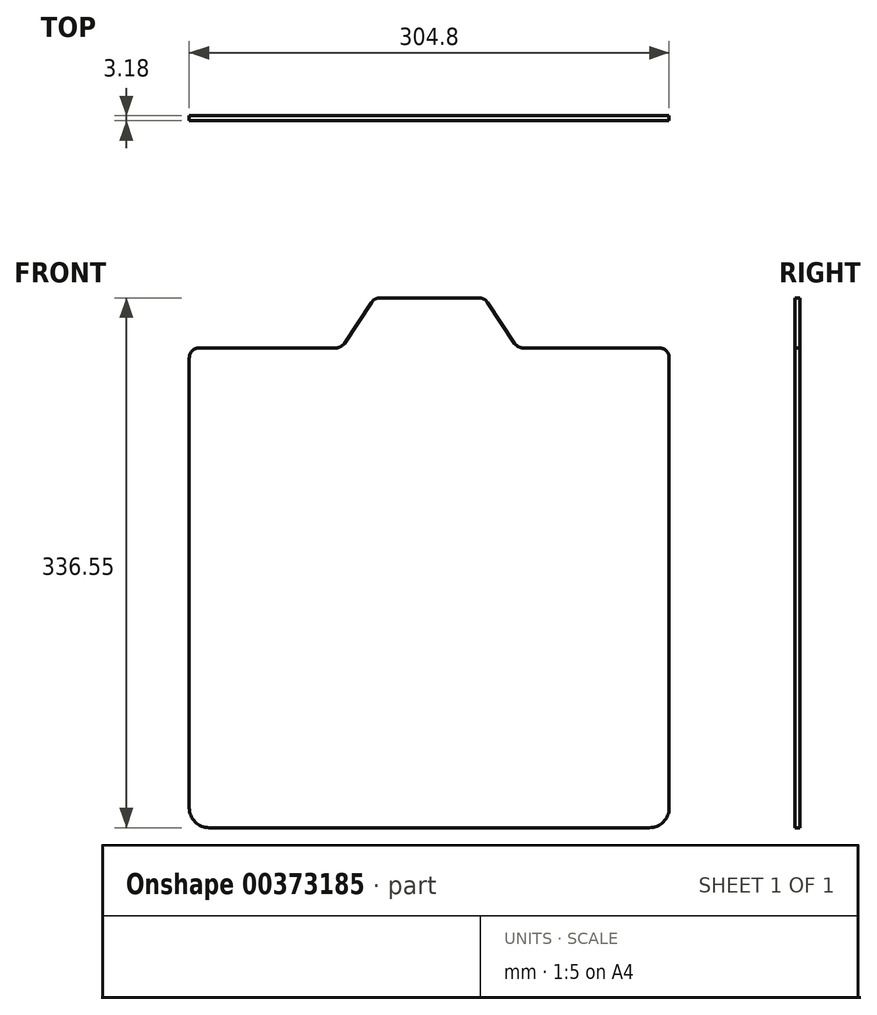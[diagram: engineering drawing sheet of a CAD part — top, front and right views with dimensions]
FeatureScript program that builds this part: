
annotation { "Feature Type Name" : "Feature", "Feature Type Description" : "" }
export const myFeature = defineFeature(function(context is Context, id is Id, definition is map)
    precondition{}
    {
        {
            var Q0;
            Q0=qCreatedBy(makeId("Front.planeOp"),FACE);
            var sketch = newSketch(context, id + "F0", { "sketchPlane" : qUnion([Q0])});
            skLineSegment(sketch, "E0.bottom", {"start": v(-152.4, 152.4) * mm, "end": v(-55.83, 152.4) * mm});
            skLineSegment(sketch, "E0.top", {"start": v(-152.4, -152.4) * mm, "end": v(152.4, -152.4) * mm});
            skLineSegment(sketch, "E0.left", {"start": v(-152.4, 152.4) * mm, "end": v(-152.4, -152.4) * mm});
            skLineSegment(sketch, "E0.right", {"start": v(152.4, 152.4) * mm, "end": v(152.4, -152.4) * mm});
            skPoint(sketch, "E0.middle", {"position": v(0, 0) * mm});
            skLineSegment(sketch, "E1.bottom", {"start": v(-34.77, 184.15) * mm, "end": v(35.08, 184.15) * mm});
            skPoint(sketch, "E1.middle", {"position": v(0, 152.4) * mm});
            skPoint(sketch, "E1.top.start.orphan", {"position": v(-35.08, 120.65) * mm});
            skPoint(sketch, "E2.orphan", {"position": v(34.77, 120.65) * mm});
            skLineSegment(sketch, "E3", {"start": v(35.08, 184.15) * mm, "end": v(56.14, 152.4) * mm});
            skLineSegment(sketch, "E4", {"start": v(-34.77, 184.15) * mm, "end": v(-55.83, 152.4) * mm});
            skLineSegment(sketch, "E5.trimOffspring", {"start": v(56.14, 152.4) * mm, "end": v(152.4, 152.4) * mm});
            skSolve(sketch);
        }
        {
            var Q0;
            Q0=makeQuery(id+"F0.imprint","IMPRINT",FACE,{"disambiguationData":[TD([[makeQuery(id+"F0.imprint","IMPRINT",EDGE,{"derivedFrom":sQuery(id+"F0.wireOp",EDGE,"E0.bottom")}),-1.0]])]});
            extrude(context, id + "F1", {"entities" : qUnion([Q0]), "endBound" : BoundingType.SYMMETRIC, "depth" : 3.17 * mm});
        }
        {
            var Q0;
            Q0=makeQuery(id+"F1.opExtrude","SWEPT_EDGE",EDGE,{"disambiguationData":[OSD([sQuery(id+"F0.wireOp",EDGE,"E0.right"),sQuery(id+"F0.wireOp",EDGE,"E5.trimOffspring")])]});
            var Q1;
            Q1=makeQuery(id+"F1.opExtrude","SWEPT_EDGE",EDGE,{"disambiguationData":[OSD([sQuery(id+"F0.wireOp",EDGE,"E0.bottom"),sQuery(id+"F0.wireOp",EDGE,"E0.left")])]});
            var Q2;
            Q2=makeQuery(id+"F1.opExtrude","SWEPT_EDGE",EDGE,{"disambiguationData":[OSD([sQuery(id+"F0.wireOp",EDGE,"E0.bottom"),sQuery(id+"F0.wireOp",EDGE,"E4")])]});
            var Q3;
            Q3=makeQuery(id+"F1.opExtrude","SWEPT_EDGE",EDGE,{"disambiguationData":[OSD([sQuery(id+"F0.wireOp",EDGE,"E1.bottom"),sQuery(id+"F0.wireOp",EDGE,"E4")])]});
            var Q4;
            Q4=makeQuery(id+"F1.opExtrude","SWEPT_EDGE",EDGE,{"disambiguationData":[OSD([sQuery(id+"F0.wireOp",EDGE,"E1.bottom"),sQuery(id+"F0.wireOp",EDGE,"E3")])]});
            var Q5;
            Q5=makeQuery(id+"F1.opExtrude","SWEPT_EDGE",EDGE,{"disambiguationData":[OSD([sQuery(id+"F0.wireOp",EDGE,"E3"),sQuery(id+"F0.wireOp",EDGE,"E5.trimOffspring")])]});
            fillet(context, id + "F2", {"entities" : qUnion([Q0, Q1, Q2, Q3, Q4, Q5]), "radius" : 6.35 * mm, "tangentPropagation" : true, "allowEdgeOverflow" : false});
        }
        {
            var Q0;
            Q0=makeQuery(id+"F1.opExtrude","SWEPT_EDGE",EDGE,{"disambiguationData":[OSD([sQuery(id+"F0.wireOp",EDGE,"E0.top"),sQuery(id+"F0.wireOp",EDGE,"E0.left")])]});
            var Q1;
            Q1=makeQuery(id+"F1.opExtrude","SWEPT_EDGE",EDGE,{"disambiguationData":[OSD([sQuery(id+"F0.wireOp",EDGE,"E0.top"),sQuery(id+"F0.wireOp",EDGE,"E0.right")])]});
            fillet(context, id + "F3", {"entities" : qUnion([Q0, Q1]), "radius" : 12.7 * mm, "tangentPropagation" : true, "allowEdgeOverflow" : false});
        }
    });
